# Revit family: ВентКлиматСтрой Вентилятор радиальный ВР 80-70
name_source: partatom
category: Оборудование
units: mm (PartAtom-declared; Revit-internal decimal feet)

## family parameters
Всегда вертикально = Да
Заголовок OmniClass = Climate Control (HVAC)
На основе рабочей плоскости = Нет
Номер OmniClass = 23.75.00.00
Общий = Нет
При загрузке вырезать с полостями = Нет
Размер круглого соединителя = Использовать диаметр
Тип детали = Нормальный
Точка расчета площади = Нет

## types (16) — shared parameters
0_О = ● : 0 - Общепромышленное
1_Ж = ● : Ж - жаростойкое
2_К = ● : К - коррозионностойкое
3_КЖ = ● : КЖ - коррозионностойкое, жаростойкое
4_В = ● : В - взрывозащищенное
5_ВК = ● : ВК - взрывозащищенное, коррозионностойкое
ADSK_Версия Revit = 2019
ADSK_Версия семейства = rev.3
ADSK_Единица измерения = шт.
ADSK_Завод-изготовитель = ООО "ЗВО ВентКлиматСтрой"
ADSK_Количество = 1
ADSK_Количество фаз = 3
Data = ВР 80-70
Data_I = DO_RV
Виброопора = Да
Классификация нагрузок = Вентиляционное оборудование
Материал корпуса = Оцинковка
Материал рамы = Металл
zero-valued in all types: ADSK_Материал тип подсчета, Oz

## per-type parameters (varying)
| type | B | C | C1 | D | L | N | O1 | R | R1 | Re | a1 | a2 | b | l |
| ВР 80-70-2,5 | 463 мм | 86 мм | 260 мм | 250 мм | 420 мм | 8 | 105 мм | 125 мм | 135 мм | 153 мм | 175 мм | 175 мм | 189 мм | 126 мм |
| ВР 80-70-2,8 | 515 мм | 96 мм | 260 мм | 280 мм | 460 мм | 8 | 120 мм | 140 мм | 155 мм | 168 мм | 195 мм | 195 мм | 212 мм | 148 мм |
| ВР 80-70-3,15 | 585 мм | 148 мм | 260 мм | 315 мм | 510 мм | 8 | 138 мм | 158 мм | 173 мм | 185 мм | 221 мм | 221 мм | 238 мм | 160 мм |
| ВР 80-70-3,55 | 645 мм | 155 мм | 340 мм | 355 мм | 535 мм | 8 | 158 мм | 178 мм | 193 мм | 205 мм | 250 мм | 250 мм | 268 мм | 175 мм |
| ВР 80-70-4 | 725 мм | 165 мм | 350 мм | 400 мм | 680 мм | 8 | 180 мм | 200 мм | 220 мм | 228 мм | 280 мм | 280 мм | 301 мм | 190 мм |
| ВР 80-70-4,5 | 825 мм | 190 мм | 380 мм | 450 мм | 750 мм | 8 | 205 мм | 225 мм | 245 мм | 253 мм | 315 мм | 315 мм | 340 мм | 207 мм |
| ВР 80-70-5 | 925 мм | 211 мм | 410 мм | 500 мм | 690 мм | 12 | 220 мм | 250 мм | 270 мм | 278 мм | 350 мм | 350 мм | 389 мм | 225 мм |
| ВР 80-70-5,6 | 1000 мм | 230 мм | 460 мм | 560 мм | 795 мм | 12 | 250 мм | 280 мм | 300 мм | 308 мм | 395 мм | 395 мм | 423 мм | 246 мм |
| ВР 80-70-6,3 | 1100 мм | 247 мм | 520 мм | 630 мм | 825 мм | 12 | 285 мм | 315 мм | 335 мм | 343 мм | 445 мм | 445 мм | 433 мм | 252 мм |
| ВР 80-70-7,1 | 1240 мм | 280 мм | 590 мм | 710 мм | 1035 мм | 16 | 315 мм | 355 мм | 375 мм | 383 мм | 500 мм | 500 мм | 488 мм | 280 мм |
| ВР 80-70-8 | 1445 мм | 316 мм | 660 мм | 800 мм | 1040 мм | 16 | 360 мм | 400 мм | 420 мм | 428 мм | 560 мм | 560 мм | 550 мм | 320 мм |
| ВР 80-70-9 | 1600 мм | 340 мм | 720 мм | 900 мм | 1165 мм | 16 | 400 мм | 450 мм | 475 мм | 485 мм | 630 мм | 630 мм | 619 мм | 350 мм |
| ВР 80-70-10 | 1810 мм | 360 мм | 840 мм | 1000 мм | 1530 мм | 16 | 450 мм | 500 мм | 525 мм | 535 мм | 700 мм | 700 мм | 688 мм | 385 мм |
| ВР 80-70-11,2 | 2060 мм | 420 мм | 1164 мм | 1120 мм | 1605 мм | 20 | 410 мм | 560 мм | 585 мм | 595 мм | 785 мм | 785 мм | 770 мм | 430 мм |
| ВР 80-70-12,5 | 2250 мм | 467 мм | 1260 мм | 1250 мм | 1720 мм | 20 | 475 мм | 625 мм | 650 мм | 660 мм | 875 мм | 875 мм | 859 мм | 492 мм |
| ВР 80-70-14 | 2510 мм | 450 мм | 1450 мм | 1400 мм | 1806 мм | 20 | 550 мм | 700 мм | 725 мм | 740 мм | 980 мм | 980 мм | 972 мм | 560 мм |
